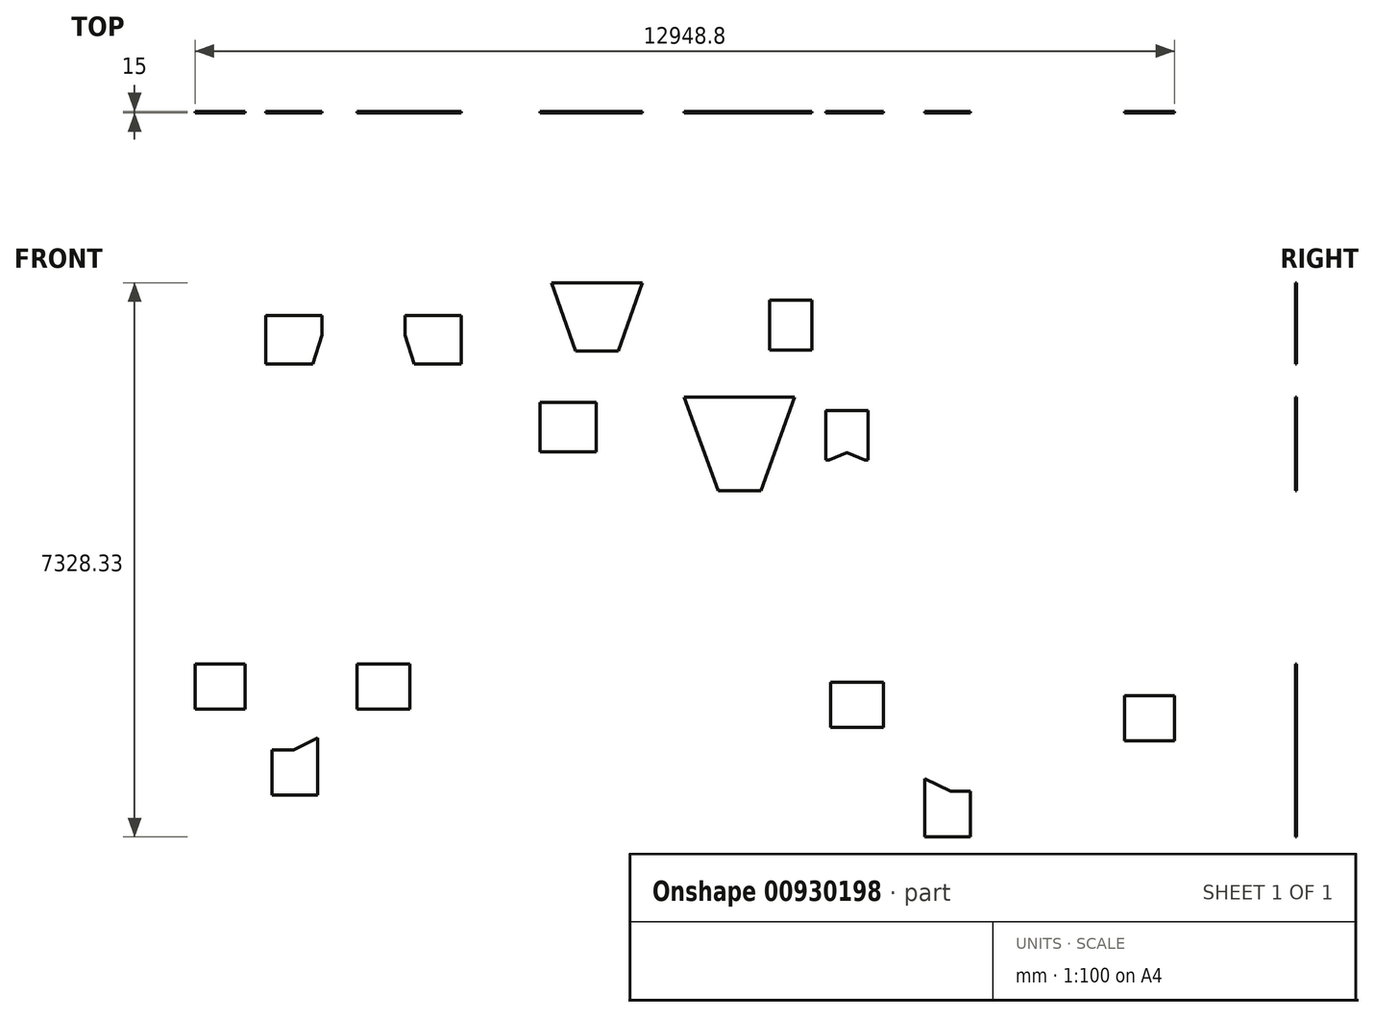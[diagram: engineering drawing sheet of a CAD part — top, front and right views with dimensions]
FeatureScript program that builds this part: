
annotation { "Feature Type Name" : "Feature", "Feature Type Description" : "" }
export const myFeature = defineFeature(function(context is Context, id is Id, definition is map)
    precondition{}
    {
        {
            var Q0;
            Q0=qCreatedBy(makeId("Front.planeOp"),FACE);
            var sketch = newSketch(context, id + "F0", { "sketchPlane" : qUnion([Q0])});
            skLineSegment(sketch, "E0", {"start": v(-197.02, 170.52) * mm, "end": v(1262.98, 170.52) * mm});
            skLineSegment(sketch, "E1", {"start": v(815.48, -1069.48) * mm, "end": v(250.48, -1069.48) * mm});
            skLineSegment(sketch, "E2", {"start": v(250.48, -1069.48) * mm, "end": v(-197.02, 170.52) * mm});
            skLineSegment(sketch, "E3", {"start": v(1262.98, 170.52) * mm, "end": v(815.48, -1069.48) * mm});
            skLineSegment(sketch, "E4", {"start": v(1674.78, -4.74) * mm, "end": v(2234.78, -4.74) * mm});
            skLineSegment(sketch, "E5", {"start": v(2234.78, -4.74) * mm, "end": v(2234.78, -664.74) * mm});
            skLineSegment(sketch, "E6", {"start": v(2234.78, -664.74) * mm, "end": v(2189.78, -664.74) * mm});
            skLineSegment(sketch, "E7", {"start": v(1674.78, -4.74) * mm, "end": v(1674.78, -664.74) * mm});
            skLineSegment(sketch, "E8", {"start": v(1674.78, -664.74) * mm, "end": v(1719.78, -664.74) * mm});
            skLineSegment(sketch, "E9", {"start": v(1949.78, -569.74) * mm, "end": v(1959.78, -569.74) * mm});
            skLineSegment(sketch, "E10", {"start": v(1959.78, -569.74) * mm, "end": v(2189.78, -664.74) * mm});
            skLineSegment(sketch, "E11", {"start": v(1949.78, -569.74) * mm, "end": v(1719.78, -664.74) * mm});
            skLineSegment(sketch, "E12.bottom", {"start": v(-2102.42, -557.17) * mm, "end": v(-1362.42, -557.17) * mm});
            skLineSegment(sketch, "E12.top", {"start": v(-2102.42, 102.83) * mm, "end": v(-1362.42, 102.83) * mm});
            skLineSegment(sketch, "E12.left", {"start": v(-2102.42, -557.17) * mm, "end": v(-2102.42, 102.83) * mm});
            skLineSegment(sketch, "E12.right", {"start": v(-1362.42, -557.17) * mm, "end": v(-1362.42, 102.83) * mm});
            skLineSegment(sketch, "E13", {"start": v(532.98, -1069.48) * mm, "end": v(532.98, -796.5) * mm, "construction": true});
            skSolve(sketch);
        }
        {
            var Q0;
            Q0 = qSketchRegion(id + "F0", true);
            extrude(context, id + "F1", {"entities" : qUnion([Q0]), "depth" : 15 * mm, "offsetDistance" : 25 * mm});
        }
        {
            var Q0;
            Q0=qCreatedBy(makeId("Front.planeOp"),FACE);
            var sketch = newSketch(context, id + "F2", { "sketchPlane" : qUnion([Q0])});
            skLineSegment(sketch, "E14", {"start": v(-1067.64, 782.15) * mm, "end": v(-1632.64, 782.15) * mm});
            skLineSegment(sketch, "E15", {"start": v(-750.14, 1682.15) * mm, "end": v(-1067.64, 782.15) * mm});
            skLineSegment(sketch, "E16.MirrorCS", {"start": v(-1950.14, 1682.15) * mm, "end": v(-1632.64, 782.15) * mm});
            skLineSegment(sketch, "E17", {"start": v(-1950.14, 1682.15) * mm, "end": v(-750.14, 1682.15) * mm});
            skLineSegment(sketch, "E18.bottom", {"start": v(931.28, 1449.75) * mm, "end": v(1491.28, 1449.75) * mm});
            skLineSegment(sketch, "E18.top", {"start": v(931.28, 789.75) * mm, "end": v(1491.28, 789.75) * mm});
            skLineSegment(sketch, "E18.left", {"start": v(931.28, 1449.75) * mm, "end": v(931.28, 789.75) * mm});
            skLineSegment(sketch, "E18.right", {"start": v(1491.28, 1449.75) * mm, "end": v(1491.28, 789.75) * mm});
            skLineSegment(sketch, "E19", {"start": v(-5727.82, 1250.93) * mm, "end": v(-4987.82, 1250.93) * mm});
            skLineSegment(sketch, "E20", {"start": v(-4987.82, 1250.93) * mm, "end": v(-4987.82, 985.93) * mm});
            skLineSegment(sketch, "E21", {"start": v(-5727.82, 1250.93) * mm, "end": v(-5727.82, 610.93) * mm});
            skLineSegment(sketch, "E22", {"start": v(-5727.82, 610.93) * mm, "end": v(-5107.82, 610.93) * mm});
            skLineSegment(sketch, "E23", {"start": v(-5107.82, 610.93) * mm, "end": v(-4987.82, 985.93) * mm});
            skLineSegment(sketch, "E24", {"start": v(-4437.25, 1463.9) * mm, "end": v(-4437.25, 299.42) * mm, "construction": true});
            skLineSegment(sketch, "E25.MirrorCS", {"start": v(-3146.7, 1250.93) * mm, "end": v(-3146.7, 610.93) * mm});
            skLineSegment(sketch, "E26.MirrorCS", {"start": v(-3146.7, 610.93) * mm, "end": v(-3766.7, 610.93) * mm});
            skLineSegment(sketch, "E27.MirrorCS", {"start": v(-3886.7, 1250.93) * mm, "end": v(-3886.7, 985.93) * mm});
            skLineSegment(sketch, "E28.MirrorCS", {"start": v(-3766.7, 610.93) * mm, "end": v(-3886.7, 985.93) * mm});
            skLineSegment(sketch, "E29.MirrorCS", {"start": v(-3146.7, 1250.93) * mm, "end": v(-3886.7, 1250.93) * mm});
            skSolve(sketch);
        }
        {
            var Q0;
            Q0 = qSketchRegion(id + "F2", true);
            extrude(context, id + "F3", {"entities" : qUnion([Q0]), "depth" : 15 * mm, "offsetDistance" : 25 * mm});
        }
        {
            var Q0;
            Q0=qCreatedBy(makeId("Front.planeOp"),FACE);
            var sketch = newSketch(context, id + "F4", { "sketchPlane" : qUnion([Q0])});
            skLineSegment(sketch, "E30.bottom", {"start": v(-6662.22, -3360.04) * mm, "end": v(-6002.22, -3360.04) * mm});
            skLineSegment(sketch, "E30.top", {"start": v(-6662.22, -3960.04) * mm, "end": v(-6002.22, -3960.04) * mm});
            skLineSegment(sketch, "E30.left", {"start": v(-6662.22, -3360.04) * mm, "end": v(-6662.22, -3960.04) * mm});
            skLineSegment(sketch, "E30.right", {"start": v(-6002.22, -3360.04) * mm, "end": v(-6002.22, -3960.04) * mm});
            skLineSegment(sketch, "E31.bottom", {"start": v(-4523.24, -3360.04) * mm, "end": v(-3823.24, -3360.04) * mm});
            skLineSegment(sketch, "E31.top", {"start": v(-4523.24, -3960.04) * mm, "end": v(-3823.24, -3960.04) * mm});
            skLineSegment(sketch, "E31.left", {"start": v(-4523.24, -3360.04) * mm, "end": v(-4523.24, -3960.04) * mm});
            skLineSegment(sketch, "E31.right", {"start": v(-3823.24, -3360.04) * mm, "end": v(-3823.24, -3960.04) * mm});
            skLineSegment(sketch, "E32", {"start": v(-5357.57, -4495.7) * mm, "end": v(-5647.57, -4495.7) * mm});
            skLineSegment(sketch, "E33", {"start": v(-5647.57, -4495.7) * mm, "end": v(-5647.57, -5095.7) * mm});
            skLineSegment(sketch, "E34", {"start": v(-5647.57, -5095.7) * mm, "end": v(-5042.57, -5095.7) * mm});
            skLineSegment(sketch, "E35", {"start": v(-5042.57, -5095.7) * mm, "end": v(-5042.57, -4335.7) * mm});
            skLineSegment(sketch, "E36", {"start": v(-5042.57, -4335.7) * mm, "end": v(-5357.57, -4495.7) * mm});
            skSolve(sketch);
        }
        {
            var Q0;
            Q0 = qSketchRegion(id + "F4", true);
            extrude(context, id + "F5", {"entities" : qUnion([Q0]), "depth" : 15 * mm, "offsetDistance" : 25 * mm});
        }
        {
            var Q0;
            Q0=qCreatedBy(makeId("Front.planeOp"),FACE);
            var sketch = newSketch(context, id + "F6", { "sketchPlane" : qUnion([Q0])});
            skLineSegment(sketch, "E37.bottom", {"start": v(1737.06, -3600.8) * mm, "end": v(2437.06, -3600.8) * mm});
            skLineSegment(sketch, "E37.top", {"start": v(1737.06, -4200.8) * mm, "end": v(2437.06, -4200.8) * mm});
            skLineSegment(sketch, "E37.left", {"start": v(1737.06, -3600.8) * mm, "end": v(1737.06, -4200.8) * mm});
            skLineSegment(sketch, "E37.right", {"start": v(2437.06, -3600.8) * mm, "end": v(2437.06, -4200.8) * mm});
            skLineSegment(sketch, "E38.bottom", {"start": v(5626.61, -3779.12) * mm, "end": v(6286.61, -3779.12) * mm});
            skLineSegment(sketch, "E38.top", {"start": v(5626.61, -4379.12) * mm, "end": v(6286.61, -4379.12) * mm});
            skLineSegment(sketch, "E38.left", {"start": v(5626.61, -3779.12) * mm, "end": v(5626.61, -4379.12) * mm});
            skLineSegment(sketch, "E38.right", {"start": v(6286.61, -3779.12) * mm, "end": v(6286.61, -4379.12) * mm});
            skLineSegment(sketch, "E39", {"start": v(2981.25, -5646.18) * mm, "end": v(3586.25, -5646.18) * mm});
            skLineSegment(sketch, "E40", {"start": v(3586.25, -5646.18) * mm, "end": v(3586.25, -5046.18) * mm});
            skLineSegment(sketch, "E41", {"start": v(3586.25, -5046.18) * mm, "end": v(3326.25, -5046.18) * mm});
            skLineSegment(sketch, "E42", {"start": v(2981.25, -5646.18) * mm, "end": v(2981.25, -4876.18) * mm});
            skLineSegment(sketch, "E43", {"start": v(2981.25, -4876.18) * mm, "end": v(3326.25, -5046.18) * mm});
            skSolve(sketch);
        }
        {
            var Q0;
            Q0 = qSketchRegion(id + "F6", true);
            extrude(context, id + "F7", {"entities" : qUnion([Q0]), "depth" : 15 * mm, "offsetDistance" : 25 * mm});
        }
    });
